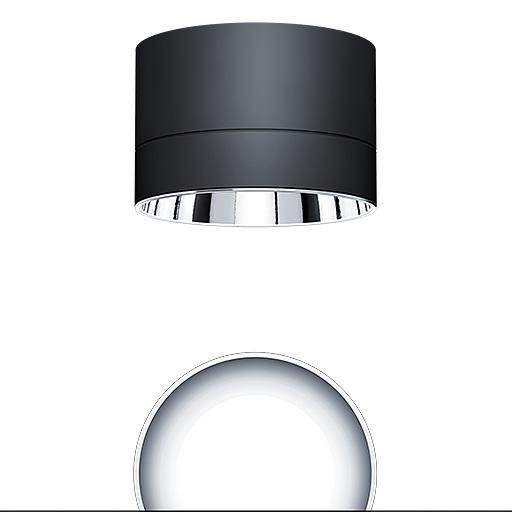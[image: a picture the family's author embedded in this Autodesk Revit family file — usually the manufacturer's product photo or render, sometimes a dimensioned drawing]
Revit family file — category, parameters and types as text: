
# Revit family: Zumtobel PANOS 3 Surface-Mounted R200
name_source: partatom
category: Lighting Fixtures
units: mm (PartAtom-declared; Revit-internal decimal feet)

## family parameters
Cut with Voids When Loaded = Yes
Host = Face
Light Source = Yes
Maintain Annotation Orientation = No
Part Type = Normal
Room Calculation Point = Yes
Round Connector Dimension = Use Diameter
Shared = No

## types (13) — shared parameters
Assembly Code = Pr_70_70_48
Color Filter = 16777215
Description = Downlight, Ceiling surface mounted luminaire
Dimming Lamp Color Temperature Shift = <None>
Emit Shape Visible in Rendering = No
Emit from Circle Diameter = 130 mm  [stored 0.426509 ft]
Lamp = LED
Luminaire Height = 128 mm  [stored 0.419948 ft]
Luminaire Length = 190 mm
Luminaire Width = 190 mm
Manufacturer = Zumtobel Lighting
Tilt Angle = -90.00°
URL = https://www.zumtobel.com
zero-valued in all types: Default Elevation

## per-type parameters (varying)
| type | Apparent Load | Material Housing | Material Housing Top | Material Reflector | Model | Photometric Web File | Power Factor | Type Image |
| PANOS SC R200 1k-940 LDO L AL BK | 10 VA | Zumtobel-Aluminium-RAL 9005-Jet Black | Zumtobel-Aluminium-RAL 9005-Jet Black | Zumtobel-Plastic-RAL 7016-Anthracite Grey-Reflective | 62930180 | 62930180_(STD_LEO).IES | 0.8 | ZS_PA3_F_SM_R200_L_AL_BKBK.jpg |
| PANOS SC R200 1k-940 LDO L AL WH | 10 VA | Zumtobel-Aluminium-RAL 9003-Signal White | Zumtobel-Aluminium-RAL 9003-Signal White | Zumtobel-Plastic-RAL 7016-Anthracite Grey-Reflective | 60819414 | 60819414_(STD_LEO).IES | 0.8 | ZS_PA3_F_SM_R200_L_AL_WHWH.jpg |
| PANOS SC R200 1k-940 LDO L SPC BK | 10 VA | Zumtobel-Aluminium-RAL 9005-Jet Black | Zumtobel-Aluminium-RAL 9005-Jet Black | Zumtobel-Plastic-RAL 7001-Silver Grey | 62930189 | 62930189_(STD_LEO).IES | 0.8 | ZS_PA3_F_SM_R200_L_SPC_BKBK.jpg |
| PANOS SC R200 1k-940 LDO L SPC WH | 10 VA | Zumtobel-Aluminium-RAL 9003-Signal White | Zumtobel-Aluminium-RAL 9003-Signal White | Zumtobel-Plastic-RAL 7001-Silver Grey | 62930171 | 62930171_(STD_LEO).IES | 0.8 | ZS_PA3_F_SM_R200_L_SPC_WHWH.jpg |
| PANOS SC R200 2k-940 LDO L AL BK | 17 VA | Zumtobel-Aluminium-RAL 9005-Jet Black | Zumtobel-Aluminium-RAL 9005-Jet Black | Zumtobel-Plastic-RAL 7016-Anthracite Grey-Reflective | 62930181 | 62930181_(STD_LEO).IES | 0.92 | ZS_PA3_F_SM_R200_L_AL_BKBK.jpg |
| PANOS SC R200 2k-940 LDO L AL WH | 17 VA | Zumtobel-Aluminium-RAL 9003-Signal White | Zumtobel-Aluminium-RAL 9003-Signal White | Zumtobel-Plastic-RAL 7016-Anthracite Grey-Reflective | 60819415 | 60819415_(STD_LEO).IES | 0.92 | ZS_PA3_F_SM_R200_L_AL_WHWH.jpg |
| PANOS SC R200 2k-940 LDO L SPC BK | 17 VA | Zumtobel-Aluminium-RAL 9005-Jet Black | Zumtobel-Aluminium-RAL 9005-Jet Black | Zumtobel-Plastic-RAL 7001-Silver Grey | 62930191 | 62930191_(STD_LEO).IES | 0.92 | ZS_PA3_F_SM_R200_L_SPC_BKBK.jpg |
| PANOS SC R200 2k-940 LDO L SPC WH | 17 VA | Zumtobel-Aluminium-RAL 9003-Signal White | Zumtobel-Aluminium-RAL 9003-Signal White | Zumtobel-Plastic-RAL 7001-Silver Grey | 62930172 | 62930172_(STD_LEO).IES | 0.92 | ZS_PA3_F_SM_R200_L_SPC_WHWH.jpg |
| PANOS SC R200 3k-930 LDO L BK BK | 25 VA | Zumtobel-Aluminium-RAL 9005-Jet Black | Zumtobel-Aluminium-RAL 9005-Jet Black | Zumtobel-Plastic-RAL 9005-Jet Black | 62930304 | 62930304_(STD_LEO).IES | 0.95 | ZS_PA3_F_SM_R200_L_BK_BKBK.jpg |
| PANOS SC R200 3k-940 LDO L AL BK | 25 VA | Zumtobel-Aluminium-RAL 9005-Jet Black | Zumtobel-Aluminium-RAL 9005-Jet Black | Zumtobel-Plastic-RAL 7016-Anthracite Grey-Reflective | 62930182 | 62930182_(STD_LEO).IES | 0.95 | ZS_PA3_F_SM_R200_L_AL_BKBK.jpg |
| PANOS SC R200 3k-940 LDO L AL WH | 25 VA | Zumtobel-Aluminium-RAL 9003-Signal White | Zumtobel-Aluminium-RAL 9003-Signal White | Zumtobel-Plastic-RAL 7016-Anthracite Grey-Reflective | 60819416 | 60819416_(STD_LEO).IES | 0.95 | ZS_PA3_F_SM_R200_L_AL_WHWH.jpg |
| PANOS SC R200 3k-940 LDO L SPC BK | 25 VA | Zumtobel-Aluminium-RAL 9005-Jet Black | Zumtobel-Aluminium-RAL 9005-Jet Black | Zumtobel-Plastic-RAL 7001-Silver Grey | 62930190 | 62930190_(STD_LEO).IES | 0.95 | ZS_PA3_F_SM_R200_L_SPC_BKBK.jpg |
| PANOS SC R200 3k-940 LDO L SPC WH | 25 VA | Zumtobel-Aluminium-RAL 9003-Signal White | Zumtobel-Aluminium-RAL 9003-Signal White | Zumtobel-Plastic-RAL 7001-Silver Grey | 62930173 | 62930173_(STD_LEO).IES | 0.95 | ZS_PA3_F_SM_R200_L_SPC_WHWH.jpg |

note: [stored X ft] marks values corroborated as IEEE doubles in the binary element streams (Revit-internal decimal feet)

## geometry (parser evidence)
native form markers: Sweep x3
no freeform markers — native parametric forms only
